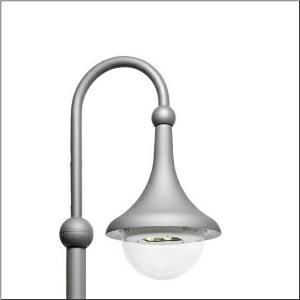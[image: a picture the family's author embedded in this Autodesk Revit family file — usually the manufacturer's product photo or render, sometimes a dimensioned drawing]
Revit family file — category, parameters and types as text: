
# Revit family: kleine_glocke_iq___st1_2a_5xa1575e1v108_a1ae
name_source: partatom
category: Lighting Fixtures
units: mm (PartAtom-declared; Revit-internal decimal feet)

## family parameters
Cut with Voids When Loaded = No
Host = Face
Light Source = No
Part Type = Normal
Room Calculation Point = No
Round Connector Dimension = Use Diameter
Shared = No

## types (1)
- --- (1 x LED, 3220 lm, 20.1 W, 3000K)
    Apparent Load = 20 VA
    CIE Flux Codes = 28 65 95 100 100
    Color Rendering = 70
    Color Temperature = 3000K
    Default Elevation = 1800 mm
    Description = Small Bell iQ, mast luminaire, primary light control with 3 zone facetted reflector, of plastic, silver coated, primary optical cover: enclosure, of PMMA, transparent, light distribution: ST1.2a, light emission: direct distribution, primary light characteristic: asymmetric, installation type: suspended mounting, High Power LED, rated luminous flux: 3.220lm, luminous efficacy: 160lm/W, light colour: 730, colour temperature: 3000K, control gear: iQ-Street Remote, D4i with power reduction, control: optimised constant luminous flux control (CLO 2.0), Desk-Remote (wireless, voltage-free reading and setting of iQ features in the workshop via application-optimized NFC function/RFID function), Light-Fading, Smart-Wire, Night-Set, Lumen-Switch, Temp-Guard, Auto-Match, Street-Remote, pre-setting: logarithmic dimming characteristic, mains connection: 230..240V, AC, 50/60Hz, start of lifetime: 20W, end of service life: 21W, reduction: 10W, luminaire housing, bell-shaped, of glass-fibre reinforced polyester, coated, Siteco® metallic grey (DB 702S), please order curved mast extension separately, diameter: 430mm, height: 575mm, mounting height: 2.5..4.0m, Smart Interface above, protection rating (complete): IP54, insulation class (complete): insulation class II (safety insulation), certification: CE, ENEC, VDE, impact resistance: IK09, standard-compliant lighting for roads and squares, packaging unit: 1 piece

Light Distribution: ST1.2a
    Height = 575 mm
    Lamp = 1 x LED
    Lamp Light Flux = 3220 lm
    Lamp Power = 20.1 W
    Lamp count = 1
    Length = 430 mm
    Luminous efficacy = 160 lm/W
    Manufacturer = Siteco
    ModVariant = No
    Model = 5XA1575E1V108
    Number of Poles = 1
    OnlyDefault = Yes
    Power Factor = 1
    Product Name = Kleine Glocke iQ | ST1.2a
    Product group = mast luminaire | pylon annexe
    ProductGroupID = 6201
    Protection Class = Protection class II
    Protection Degree = IP 54
    RLX_Detail_Level = 1
    RLX_Emergency_Light_Flux = 0 lm
    RLX_Emergency_Type = 0
    RLX_Emergency_Type_DB = No
    RlxData = <blob elided: 73585 chars, md5=d7633016>
    Socket = socket
    Standby Power = 0 W
    System Light Flux = 3220 lm
    System Power = 20 W
    Type Comments = factory setting: luminous flux: 100 % | dim-lin: 254 | 376 mA
    Type Image = l_1347699.jpg
    URL = http://relux.com
    VarID = @adj_060006
    Voltage = 0 V
    Weight = 0.00 kg
    Width = 0 mm  [stored 0 ft]

note: [stored X ft] marks values corroborated as IEEE doubles in the binary element streams (Revit-internal decimal feet)

## geometry (parser evidence)
native form markers: Blend x4, Sweep x10
no freeform markers — native parametric forms only
